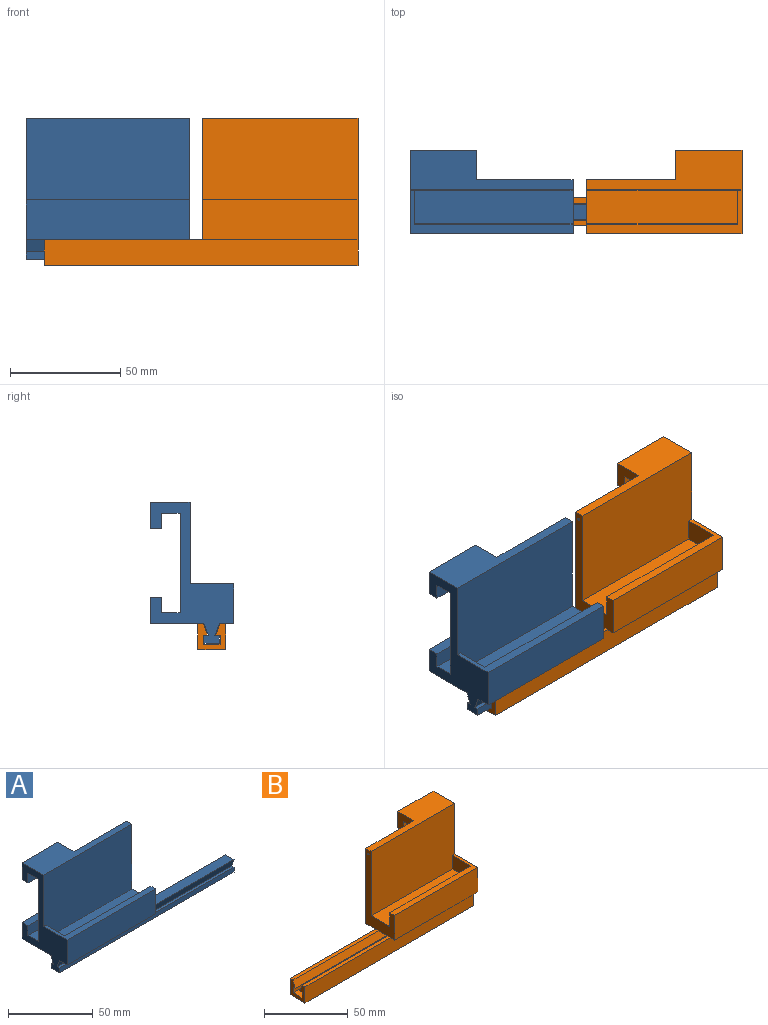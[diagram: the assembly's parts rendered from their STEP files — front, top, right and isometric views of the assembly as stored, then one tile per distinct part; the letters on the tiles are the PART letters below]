
ASSEMBLY  parts=2 mates=1
PART A: 34 faces, bbox 146x37.8x64 mm
  f0: plane 74x18mm, normal (0,-1,0), area 1332mm2, adj f2,f4,f17,f29
  f1: plane 74x24.33mm, normal (0,0,-1), area 1206.5mm2, adj f4,f8,f9,f15,f23,f29
  f2: plane 74x6.47mm, normal (0,0,-1), area 478.7mm2, adj f0,f4,f22,f29
  f3: plane 74x18mm, normal (0,0,1), area 738mm2, adj f4,f5,f8,f10,f12,f29
  f4: plane 64x37.8mm, normal (-1,0,0), area 860.9mm2, adj f0,f1,f2,f3,f5,f6,f7,f8
  f5: plane 74x47mm, normal (0,-1,0), area 3458mm2, adj f3,f4,f17,f18,f29,f33
  f6: plane 30x8.5mm, normal (0,0,-1), area 255mm2, adj f4,f8,f10,f11
  f7: plane 30x8.5mm, normal (0,0,1), area 255mm2, adj f4,f8,f9,f14
  f8: plane 74x55mm, normal (0,1,0), area 3770mm2, adj f1,f3,f4,f6,f7,f9,f10,f29
  f9: plane 13.5x12mm, normal (1,0,0), area 102.5mm2, adj f1,f7,f8,f14,f15,f16
  f10: plane 13.5x12mm, normal (1,0,0), area 102.5mm2, adj f3,f6,f8,f11,f12,f13
  f11: plane 30x7mm, normal (0,-1,0), area 210mm2, adj f4,f6,f10,f13
  f12: plane 30x12mm, normal (0,1,0), area 360mm2, adj f3,f4,f10,f13
  f13: plane 30x5mm, normal (0,0,-1), area 150mm2, adj f4,f10,f11,f12
  f14: plane 30x7mm, normal (0,-1,0), area 210mm2, adj f4,f7,f9,f16
  f15: plane 30x12mm, normal (0,1,0), area 360mm2, adj f1,f4,f9,f16
  f16: plane 30x5mm, normal (0,0,1), area 150mm2, adj f4,f9,f14,f15
  f17: plane 74x19.8mm, normal (0,0,1), area 327.6mm2, adj f0,f4,f5,f19,f29,f33
  f18: plane 72x15mm, normal (0,0,1), area 1080mm2, adj f5,f20,f29,f33
  f19: plane 72x9.2mm, normal (0,1,0), area 662.4mm2, adj f17,f20,f29,f33
  f20: cylinder r=0.8mm len=72mm, axis (-1,0,0), area 90.5mm2, adj f18,f19,f29,f33
  f21: plane 146x2mm, normal (0,0,1), area 292mm2, adj f4,f22,f27,f32
  f22: plane 146x5.5mm, normal (0,-0.94,-0.34), area 854.4mm2, adj f2,f4,f21,f28,f32
  f23: plane 146x5.5mm, normal (0,0.94,-0.34), area 854.4mm2, adj f1,f4,f24,f28,f32
  f24: plane 146x2mm, normal (0,0,1), area 292mm2, adj f4,f23,f25,f32
  f25: plane 146x3.5mm, normal (0,1,0), area 511mm2, adj f4,f24,f26,f32
  f26: plane 146x7mm, normal (0,0,-1), area 1022mm2, adj f4,f25,f27,f32
  f27: plane 146x3.5mm, normal (0,-1,0), area 511mm2, adj f4,f21,f26,f32
  f28: plane 72x7mm, normal (0,0,1), area 504mm2, adj f22,f23,f29,f32
  f29: plane 55x24.3mm, normal (1,0,0), area 445.3mm2, adj f0,f1,f2,f3,f5,f8,f17,f18
  f30: cylinder r=0.5mm len=20mm, axis (1,0,0), area 62.8mm2, adj f29,f31
  f31: plane 1x1mm, normal (1,0,0), area 0.8mm2, adj f30
  f32: plane 9x7mm, normal (1,0,0), area 52mm2, adj f21,f22,f23,f24,f25,f26,f27,f28
  f33: plane 15.8x10mm, normal (1,0,0), area 157.9mm2, adj f5,f17,f18,f19,f20
PART B: 39 faces, bbox 142.5x37.8x66.8 mm
  f0: plane 70.5x47mm, normal (0,-1,0), area 3293.5mm2, adj f4,f6,f9,f12,f34,f38
  f1: plane 70.5x21.51mm, normal (0,0,-1), area 969.9mm2, adj f5,f12,f13,f19,f26,f34
  f2: plane 70.5x7.64mm, normal (0,0,-1), area 538.5mm2, adj f12,f23,f27,f34
  f3: plane 70.5x3.65mm, normal (0,0,-1), area 257.3mm2, adj f12,f21,f24,f34
  f4: plane 70.5x18mm, normal (0,0,1), area 722.2mm2, adj f0,f5,f12,f14,f16,f34
  f5: plane 70.5x55mm, normal (0,1,0), area 3577.5mm2, adj f1,f4,f10,f11,f12,f13,f14,f34
  f6: plane 70.5x19.8mm, normal (0,0,1), area 313.6mm2, adj f0,f7,f12,f21,f34,f38
  f7: plane 68.5x9.2mm, normal (0,1,0), area 630.2mm2, adj f6,f8,f34,f38
  f8: cylinder r=0.8mm len=68.5mm, axis (-1,0,0), area 86.1mm2, adj f7,f9,f34,f38
  f9: plane 68.5x15mm, normal (0,0,1), area 1027.5mm2, adj f0,f8,f34,f38
  f10: plane 30x8.5mm, normal (0,0,-1), area 255mm2, adj f5,f12,f14,f15
  f11: plane 30x8.5mm, normal (0,0,1), area 255mm2, adj f5,f12,f13,f18
  f12: plane 66.8x37.8mm, normal (1,0,0), area 897mm2, adj f0,f1,f2,f3,f4,f5,f6,f10
  f13: plane 13.5x12mm, normal (-1,0,0), area 102.5mm2, adj f1,f5,f11,f18,f19,f20
  f14: plane 13.5x12mm, normal (-1,0,0), area 102.5mm2, adj f4,f5,f10,f15,f16,f17
  f15: plane 30x7mm, normal (0,-1,0), area 210mm2, adj f10,f12,f14,f17
  f16: plane 30x12mm, normal (0,1,0), area 360mm2, adj f4,f12,f14,f17
  f17: plane 30x5mm, normal (0,0,-1), area 150mm2, adj f12,f14,f15,f16
  f18: plane 30x7mm, normal (0,-1,0), area 210mm2, adj f11,f12,f13,f20
  f19: plane 30x12mm, normal (0,1,0), area 360mm2, adj f1,f12,f13,f20
  f20: plane 30x5mm, normal (0,0,1), area 150mm2, adj f12,f13,f18,f19
  f21: plane 70.5x18mm, normal (0,-1,0), area 1269mm2, adj f3,f6,f12,f34
  f22: plane 142.5x1.87mm, normal (0,0,-1), area 266.7mm2, adj f12,f23,f31,f37
  f23: plane 142.5x5.2mm, normal (0,0.94,0.34), area 788.5mm2, adj f2,f12,f22,f33,f37
  f24: plane 142.5x11.8mm, normal (0,-1,0), area 1681.5mm2, adj f3,f12,f25,f33,f37
  f25: plane 142.5x12.64mm, normal (0,0,-1), area 1801mm2, adj f12,f24,f26,f37
  f26: plane 142.5x11.8mm, normal (0,1,0), area 1681.5mm2, adj f1,f12,f25,f32,f37
  f27: plane 142.5x5.2mm, normal (0,-0.94,0.34), area 788.5mm2, adj f2,f12,f28,f32,f37
  f28: plane 142.5x1.87mm, normal (0,0,-1), area 266.7mm2, adj f12,f27,f29,f37
  f29: plane 142.5x4.1mm, normal (0,-1,0), area 584.2mm2, adj f12,f28,f30,f37
  f30: plane 142.5x7.6mm, normal (0,0,1), area 1083mm2, adj f12,f29,f31,f37
  f31: plane 142.5x4.1mm, normal (0,1,0), area 584.2mm2, adj f12,f22,f30,f37
  f32: plane 72x2.5mm, normal (0,0,1), area 180mm2, adj f26,f27,f34,f37
  f33: plane 72x2.5mm, normal (0,0,1), area 180mm2, adj f23,f24,f34,f37
  f34: plane 55x24.3mm, normal (-1,0,0), area 445.3mm2, adj f0,f1,f2,f3,f4,f5,f6,f7
  f35: cylinder r=0.5mm len=20mm, axis (-1,0,0), area 62.8mm2, adj f34,f36
  f36: plane 1x1mm, normal (-1,0,0), area 0.8mm2, adj f35
  f37: plane 12.64x11.8mm, normal (-1,0,0), area 88.1mm2, adj f22,f23,f24,f25,f26,f27,f28,f29
  f38: plane 15.8x10mm, normal (-1,0,0), area 157.9mm2, adj f0,f6,f7,f8,f9
PLACE A t=(-40.19,28.24,20.77)mm fixed
PLACE B rot(axis=(0,0,-1),0deg) t=(-44.48,28.24,20.77)mm
MATE slider B.f35 <-> A.f30  axis (-1,0,0) through (-37.48,17.49,45.27)mm
